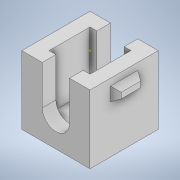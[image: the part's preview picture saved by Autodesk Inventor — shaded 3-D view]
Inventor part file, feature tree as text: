
AUTODESK INVENTOR PART (.ipt)
format: ipt  version: 2022 (Build 260153000, 153)  size: 139,264 bytes
history: native  units: in
note: dims shown in document units (in); Inventor stores cm internally (conversion verified against a paired STEP export)
features: sketch x9, extrude x4, shell x1
ambient origin geometry x8: Origin, YZ Plane, XZ Plane, XY Plane, X Axis, Y Axis, Z Axis, Center Point
bodies: Solid1 (feature_tree)
feature tree (14):
  extrude  "Extrusion1"  Depth=0.1969in
  shell  "Shell1"  Thickness=0.1969in
  extrude  "Extrusion3"  TaperAngle=0.0deg  [1 undecoded]
  sketch  "Sketch4"  dims[d10=0.0394in d11=0.0197in d12=-0.2061in]
  sketch  "Sketch5"  dims[d13=0.0394in d14=0.0787in]
  sketch  "Sketch6"  dims[d15=0.0394in]
  sketch  "Sketch7"  dims[d16=0.0787in]
  sketch  "Sketch8"  dims[d17=0.0394in]
  extrude  "Extrusion4"  Depth=0.0197in
  extrude  "Extrusion5"  Depth=0.0394in
  sketch  "Sketch1"  dims[d0=0.1969in d1=0.1969in d2=0.1969in d3=0.0in]
  sketch  "Sketch3"  dims[d4=0.0394in d8=0.0in d9=0.0in]
  sketch  "Sketch9"  dims[d18=0.0197in d19=-0.2061in]
  sketch  "Sketch10"
note: 1 required parameter value undecoded (feature->parameter linkage not recoverable at this tier; creation-order binding heuristic only, values carry confidence <= 0.55)
